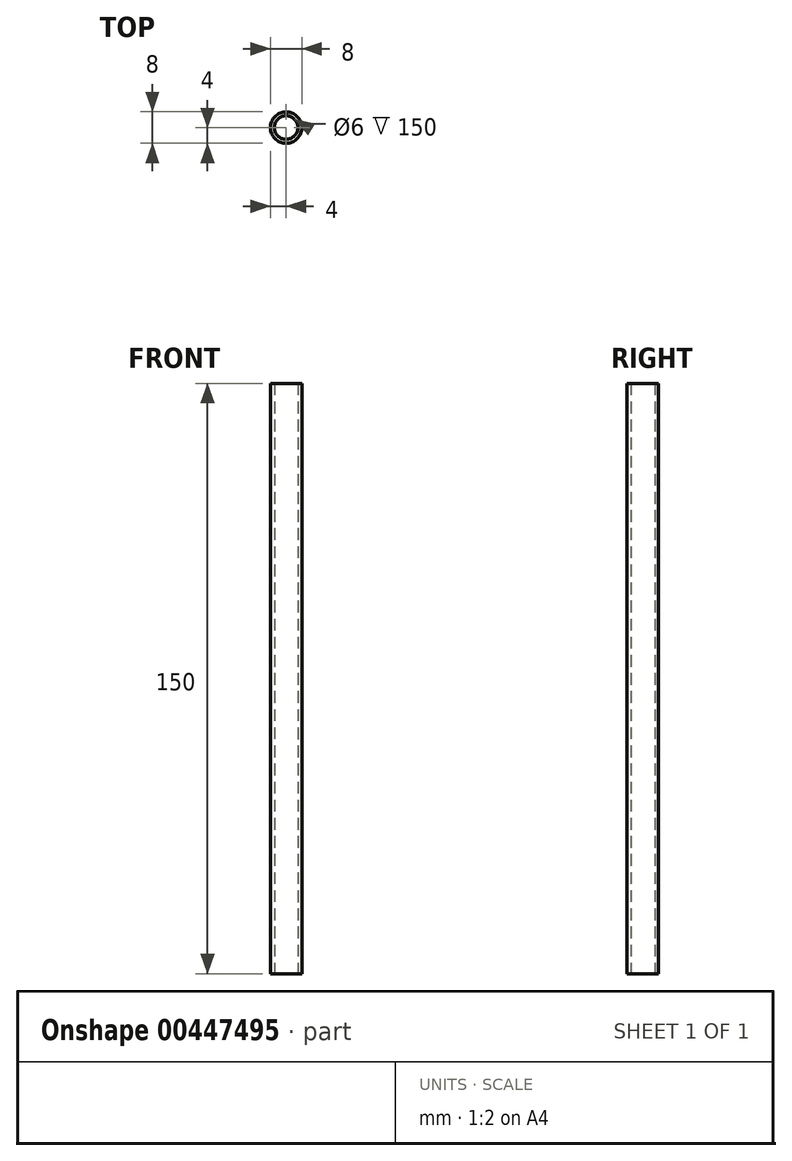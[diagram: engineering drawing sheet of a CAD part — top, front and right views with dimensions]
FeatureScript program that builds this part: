
annotation { "Feature Type Name" : "Feature", "Feature Type Description" : "" }
export const myFeature = defineFeature(function(context is Context, id is Id, definition is map)
    precondition{}
    {
        {
            var Q0;
            Q0=qCreatedBy(makeId("Top.planeOp"),FACE);
            var sketch = newSketch(context, id + "F0", { "sketchPlane" : qUnion([Q0])});
            skCircle(sketch, "E0", {"center": v(0, 0) * mm, "radius": 3 * mm});
            skCircle(sketch, "E1", {"center": v(0, 0) * mm, "radius": 4 * mm});
            skSolve(sketch);
        }
        {
            var Q0;
            Q0 = qSketchRegion(id + "F0", true);
            extrude(context, id + "F1", {"entities" : qUnion([Q0]), "depth" : 150 * mm});
        }
    });
